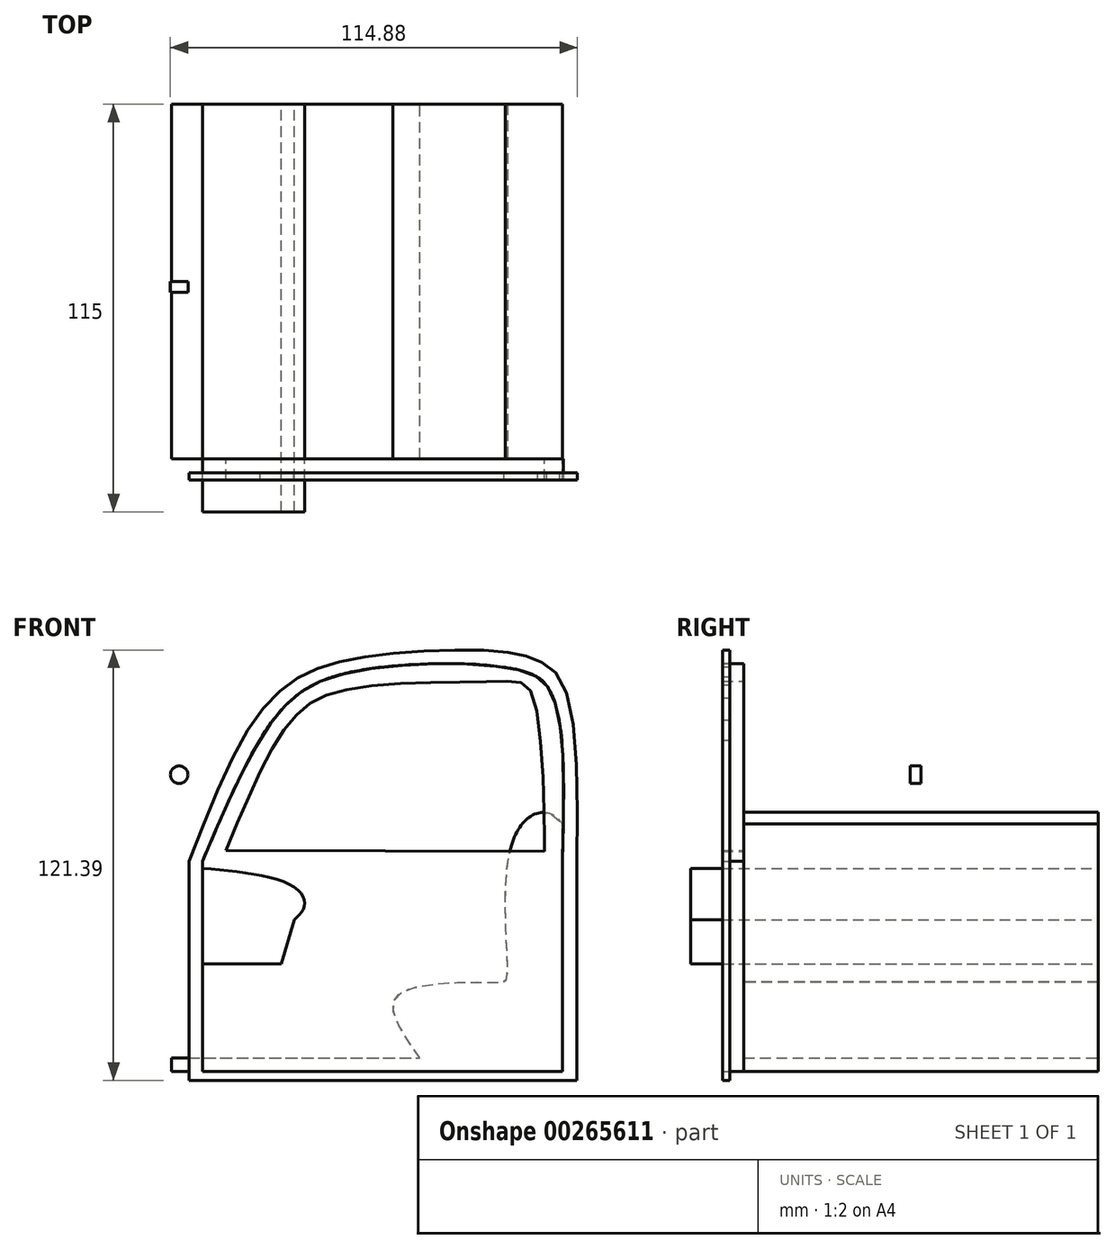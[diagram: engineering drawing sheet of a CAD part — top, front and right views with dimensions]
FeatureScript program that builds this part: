
annotation { "Feature Type Name" : "Feature", "Feature Type Description" : "" }
export const myFeature = defineFeature(function(context is Context, id is Id, definition is map)
    precondition{}
    {
        {
            var Q0;
            Q0=qCreatedBy(makeId("Front.planeOp"),FACE);
            var sketch = newSketch(context, id + "F0", { "sketchPlane" : qUnion([Q0])});
            skLineSegment(sketch, "E0.bottom", {"start": v(-52.37, -30.32) * mm, "end": v(58, -30.32) * mm});
            skLineSegment(sketch, "E0.top", {"start": v(-52.37, 75.93) * mm, "end": v(58, 75.93) * mm});
            skLineSegment(sketch, "E0.left", {"start": v(-52.37, -30.32) * mm, "end": v(-52.37, 75.93) * mm});
            skLineSegment(sketch, "E0.right", {"start": v(58, -30.32) * mm, "end": v(58, 75.93) * mm});
            skLineSegment(sketch, "E1", {"start": v(-52.37, -26.56) * mm, "end": v(17.83, -26.56) * mm});
            skFitSpline(sketch, "E2", {"points": [v(17.83, -26.56) * mm, v(11.64, -8.73) * mm, v(39.8, -5.16) * mm, v(42.43, -3.66) * mm, v(45.05, 37.08) * mm, v(58, 39.52) * mm, v(58, 9.86) * mm], "startDerivative": vector(-102.72, 146.21) * mm, "endDerivative": vector(-61.38, 44.33) * mm});
            skSolve(sketch);
        }
        {
            var Q0;
            {var subQ2=sQuery(id+"F0.wireOp",EDGE,"E0.bottom");Q0=makeQuery(id+"F0.imprint","IMPRINT",FACE,{"disambiguationData":[TD([[makeQuery(id+"F0.imprint","IMPRINT",EDGE,{"derivedFrom":subQ2}),1.0]])]});}
            extrude(context, id + "F1", {"entities" : qUnion([Q0]), "endBound" : BoundingType.SYMMETRIC, "depth" : 100 * mm});
        }
        {
            var Q0;
            Q0=makeQuery(id+"F1.opExtrude","CAP_FACE",FACE,{"disambiguationData":[OSD([sQuery(id+"F0.wireOp",EDGE,"E0.bottom"),sQuery(id+"F0.wireOp",EDGE,"E0.left"),sQuery(id+"F0.wireOp",EDGE,"E0.right"),sQuery(id+"F0.wireOp",EDGE,"E1"),sQuery(id+"F0.wireOp",EDGE,"E2")])],"isStart":true});
            var sketch = newSketch(context, id + "F2", { "sketchPlane" : qUnion([Q0])});
            skLineSegment(sketch, "E3.bottom", {"start": v(-35.3, -30.32) * mm, "end": v(30.41, -30.32) * mm});
            skLineSegment(sketch, "E3.top", {"start": v(-35.3, 0) * mm, "end": v(21.37, 0) * mm});
            skLineSegment(sketch, "E3.left", {"start": v(-35.3, -30.32) * mm, "end": v(-35.3, 0) * mm});
            skLineSegment(sketch, "E4", {"start": v(21.37, 0) * mm, "end": v(17.65, 12.48) * mm});
            skFitSpline(sketch, "E5", {"points": [v(17.65, 12.48) * mm, v(14.83, 16.43) * mm, v(17.65, 21.68) * mm, v(43.55, 26.94) * mm, v(64.2, 27.5) * mm], "startDerivative": vector(-24.47, 23.82) * mm, "endDerivative": vector(59, 0.05) * mm});
            skLineSegment(sketch, "E6", {"start": v(43.55, 26.94) * mm, "end": v(43.55, -30.32) * mm});
            skLineSegment(sketch, "E7", {"start": v(43.55, -30.32) * mm, "end": v(30.41, -30.32) * mm});
            skPoint(sketch, "E3.right.end.orphan", {"position": v(30.41, 0) * mm});
            skLineSegment(sketch, "E8", {"start": v(21.37, 0) * mm, "end": v(43.55, 0) * mm});
            skSolve(sketch);
        }
        {
            var Q0;
            Q0=makeQuery(id+"F2.imprint","IMPRINT",FACE,{"disambiguationData":[TD([[makeQuery(id+"F2.imprint","IMPRINT",EDGE,{"derivedFrom":sQuery(id+"F2.wireOp",EDGE,"E4")}),-1.0]])]});
            extrude(context, id + "F3", {"entities" : qUnion([Q0]), "oppositeDirection" : true, "depth" : 115 * mm});
        }
        {
            var Q0;
            Q0=makeQuery(id+"F1.opExtrude","CAP_FACE",FACE,{"disambiguationData":[OSD([sQuery(id+"F0.wireOp",EDGE,"E0.bottom"),sQuery(id+"F0.wireOp",EDGE,"E0.left"),sQuery(id+"F0.wireOp",EDGE,"E0.right"),sQuery(id+"F0.wireOp",EDGE,"E1"),sQuery(id+"F0.wireOp",EDGE,"E2")])],"isStart":false});
            var sketch = newSketch(context, id + "F4", { "sketchPlane" : qUnion([Q0])});
            skLineSegment(sketch, "E9.bottom", {"start": v(58, -30.32) * mm, "end": v(-43.55, -30.32) * mm});
            skLineSegment(sketch, "E9.left", {"start": v(58, -30.32) * mm, "end": v(58, 29) * mm});
            skLineSegment(sketch, "E9.right", {"start": v(-43.55, -30.32) * mm, "end": v(-43.55, 29) * mm});
            skFitSpline(sketch, "E10", {"points": [v(-43.55, 29) * mm, v(-22.9, 69.74) * mm, v(-1.88, 82.32) * mm, v(43.36, 83.44) * mm, v(55.2, 75.75) * mm, v(58, 29) * mm], "startDerivative": vector(85.44, 201.79) * mm, "endDerivative": vector(-6.45, -241.46) * mm});
            skFitSpline(sketch, "E11", {"points": [v(-36.92, 32) * mm, v(-19.34, 67.67) * mm, v(-1.88, 77.62) * mm, v(40.92, 79.69) * mm, v(49.75, 75.37) * mm, v(52.94, 31.82) * mm, v(52.94, 31.63) * mm], "startDerivative": vector(74.67, 181.05) * mm, "endDerivative": vector(0.05, -3.93) * mm});
            skLineSegment(sketch, "E12", {"start": v(-36.92, 32) * mm, "end": v(52.94, 31.82) * mm});
            skSolve(sketch);
        }
        {
            var Q0;
            Q0 = qSketchRegion(id + "F4", true);
            extrude(context, id + "F5", {"entities" : qUnion([Q0]), "depth" : 6 * mm});
        }
        {
            var Q0;
            Q0=makeQuery(id+"F5.opExtrude","CAP_FACE",FACE,{"disambiguationData":[OSD([sQuery(id+"F4.wireOp",EDGE,"E9.bottom"),sQuery(id+"F4.wireOp",EDGE,"E9.left"),sQuery(id+"F4.wireOp",EDGE,"E9.right"),sQuery(id+"F4.wireOp",EDGE,"E10"),sQuery(id+"F4.wireOp",EDGE,"E11"),sQuery(id+"F4.wireOp",EDGE,"E12")])],"isStart":false});
            var sketch = newSketch(context, id + "F6", { "sketchPlane" : qUnion([Q0])});
            skLineSegment(sketch, "E13.top", {"start": v(-47.37, -32.82) * mm, "end": v(62.16, -32.82) * mm});
            skLineSegment(sketch, "E13.left", {"start": v(-47.37, 29) * mm, "end": v(-47.37, -32.82) * mm});
            skLineSegment(sketch, "E13.right", {"start": v(62.16, 29) * mm, "end": v(62.16, -32.82) * mm});
            skFitSpline(sketch, "E14", {"points": [v(-47.37, 29) * mm, v(-31.58, 64.72) * mm, v(-19.39, 78.91) * mm, v(-6.2, 84.9) * mm, v(16.79, 88.1) * mm, v(41.38, 88.1) * mm, v(50.97, 85.7) * mm, v(58.39, 78.67) * mm, v(62.16, 29) * mm], "startDerivative": vector(92.74, 238.3) * mm, "endDerivative": vector(-2.8, -324.84) * mm});
            skLineSegment(sketch, "E15.top", {"start": v(-43.55, -30.32) * mm, "end": v(58, -30.32) * mm});
            skLineSegment(sketch, "E15.left", {"start": v(-43.55, 29) * mm, "end": v(-43.55, -30.32) * mm});
            skLineSegment(sketch, "E15.right", {"start": v(58, 29) * mm, "end": v(58, -30.32) * mm});
            skFitSpline(sketch, "E16", {"points": [v(-43.55, 29) * mm, v(-27.48, 63) * mm, v(-17.96, 74.99) * mm, v(-6.2, 81.2) * mm, v(16.79, 84.53) * mm, v(41.38, 83.75) * mm, v(50.97, 80.93) * mm, v(53.48, 78.67) * mm, v(57.1, 68.74) * mm, v(58, 29) * mm], "startDerivative": vector(103.55, 237.38) * mm, "endDerivative": vector(-7.28, -274.99) * mm});
            skSolve(sketch);
        }
        {
            var Q0;
            Q0=makeQuery(id+"F6.imprint","IMPRINT",FACE,{"disambiguationData":[TD([[makeQuery(id+"F6.imprint","IMPRINT",EDGE,{"derivedFrom":sQuery(id+"F6.wireOp",EDGE,"E13.top")}),1.0]])]});
            var Q1;
            Q1=sQuery(id+"F6.wireOp",EDGE,"E14");
            var Q2;
            Q2=sQuery(id+"F6.wireOp",EDGE,"E16");
            var Q3;
            Q3=sQuery(id+"F6.wireOp",EDGE,"E15.right");
            var Q4;
            Q4=sQuery(id+"F6.wireOp",EDGE,"E13.right");
            var Q5;
            Q5=sQuery(id+"F6.wireOp",EDGE,"E15.top");
            var Q6;
            Q6=sQuery(id+"F6.wireOp",EDGE,"E13.top");
            var Q7;
            Q7=sQuery(id+"F6.wireOp",EDGE,"E13.left");
            var Q8;
            Q8=sQuery(id+"F6.wireOp",EDGE,"E15.left");
            extrude(context, id + "F7", {"entities" : qUnion([Q0]), "surfaceEntities" : qUnion([Q1, Q2, Q3, Q4, Q5, Q6, Q7, Q8]), "oppositeDirection" : true, "depth" : 2 * mm});
        }
        {
            var Q0;
            Q0=qCreatedBy(makeId("Front.planeOp"),FACE);
            var sketch = newSketch(context, id + "F8", { "sketchPlane" : qUnion([Q0])});
            skCircle(sketch, "E17", {"center": v(-50.16, 53.39) * mm, "radius": 2.48 * mm});
            skSolve(sketch);
        }
        {
            var Q0;
            Q0 = qSketchRegion(id + "F8", true);
            extrude(context, id + "F9", {"entities" : qUnion([Q0]), "depth" : 3 * mm});
        }
    });
